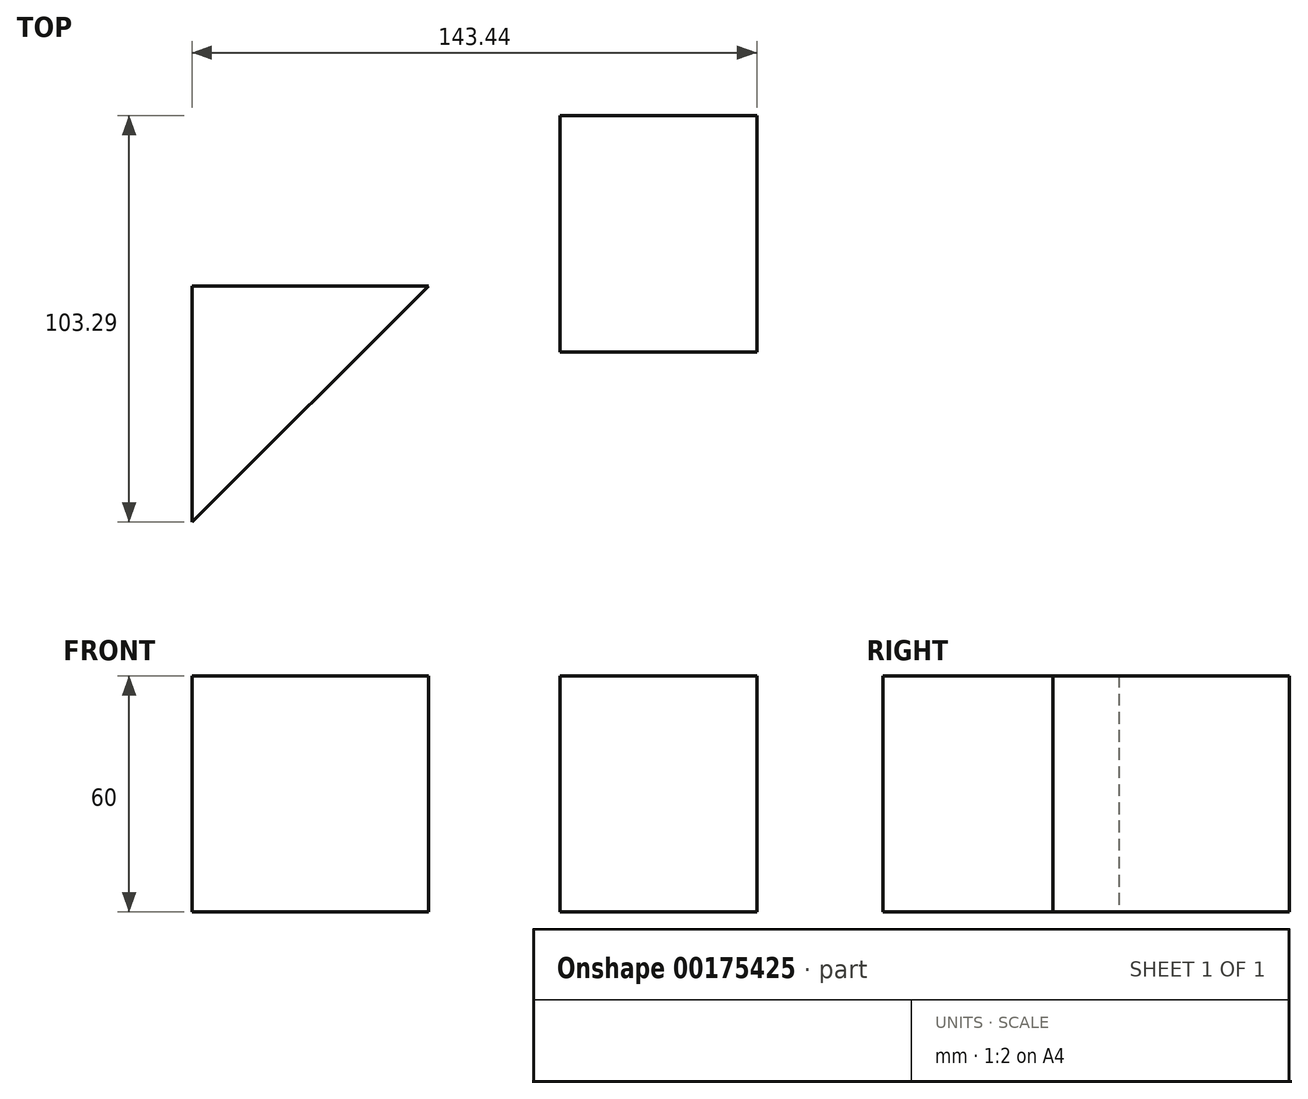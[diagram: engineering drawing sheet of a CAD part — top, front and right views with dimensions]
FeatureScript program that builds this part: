
annotation { "Feature Type Name" : "Feature", "Feature Type Description" : "" }
export const myFeature = defineFeature(function(context is Context, id is Id, definition is map)
    precondition{}
    {
        {
            var Q0;
            Q0=qCreatedBy(makeId("Top.planeOp"),FACE);
            var sketch = newSketch(context, id + "F0", { "sketchPlane" : qUnion([Q0])});
            skLineSegment(sketch, "E0.bottom", {"start": v(-23.73, 36.37) * mm, "end": v(26.27, 36.37) * mm});
            skLineSegment(sketch, "E0.top", {"start": v(-23.73, -23.63) * mm, "end": v(26.27, -23.63) * mm});
            skLineSegment(sketch, "E0.left", {"start": v(-23.73, 36.37) * mm, "end": v(-23.73, -23.63) * mm});
            skLineSegment(sketch, "E0.right", {"start": v(26.27, 36.37) * mm, "end": v(26.27, -23.63) * mm});
            skSolve(sketch);
        }
        {
            var Q0;
            Q0 = qSketchRegion(id + "F0", true);
            extrude(context, id + "F1", {"entities" : qUnion([Q0]), "depth" : 60 * mm});
        }
        {
            var Q0;
            Q0=qCreatedBy(makeId("Top.planeOp"),FACE);
            var sketch = newSketch(context, id + "F2", { "sketchPlane" : qUnion([Q0])});
            skLineSegment(sketch, "E1.bottom", {"start": v(-117.17, -6.92) * mm, "end": v(-57.17, -6.92) * mm});
            skLineSegment(sketch, "E1.left", {"start": v(-117.17, -6.92) * mm, "end": v(-117.17, -66.92) * mm});
            skLineSegment(sketch, "E2", {"start": v(-57.17, -6.92) * mm, "end": v(-117.17, -66.92) * mm});
            skPoint(sketch, "E1.right.end.orphan", {"position": v(-57.17, -66.92) * mm});
            skSolve(sketch);
        }
        {
            var Q0;
            Q0=makeQuery(id+"F2.imprint","IMPRINT",FACE,{"disambiguationData":[TD([[makeQuery(id+"F2.imprint","IMPRINT",EDGE,{"derivedFrom":sQuery(id+"F2.wireOp",EDGE,"E1.bottom")}),-1.0]])]});
            extrude(context, id + "F3", {"entities" : qUnion([Q0]), "depth" : 60 * mm});
        }
    });
